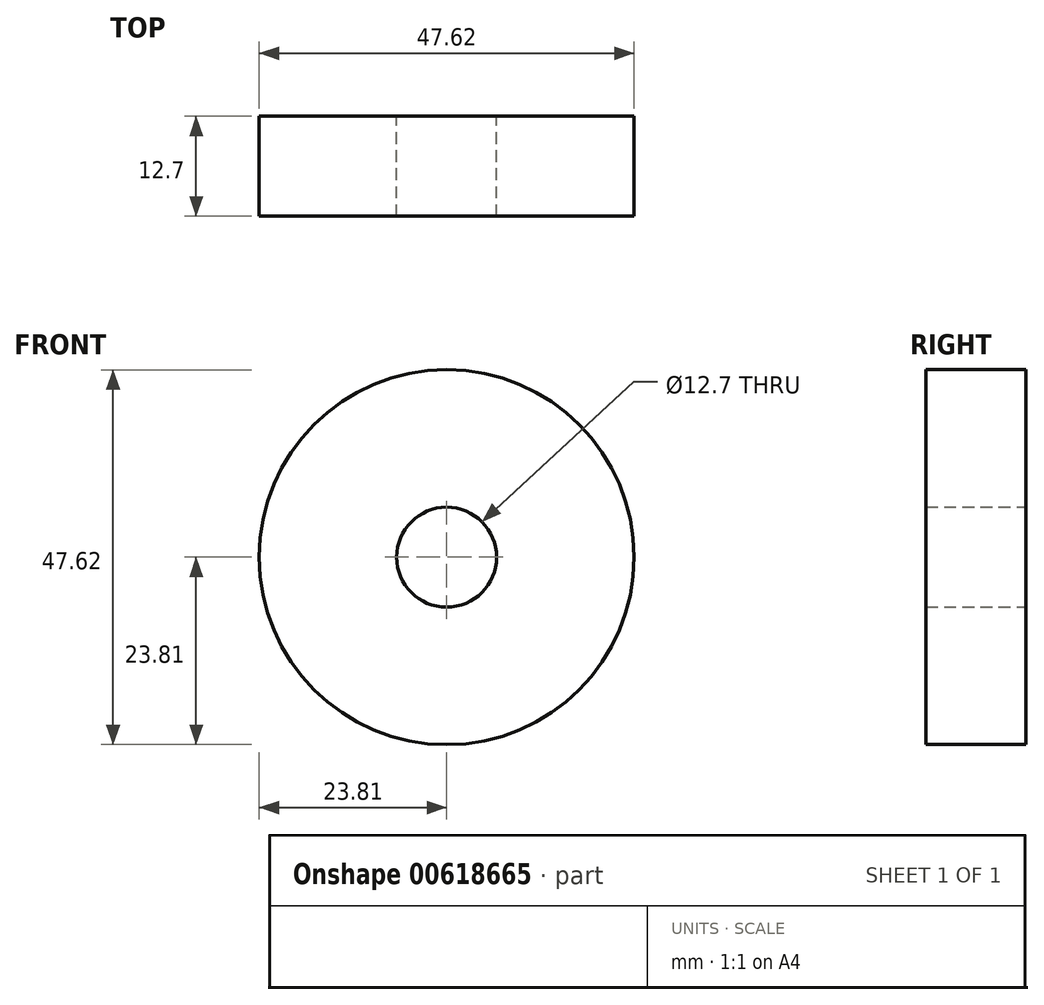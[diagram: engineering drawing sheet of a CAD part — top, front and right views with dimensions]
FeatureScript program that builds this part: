
annotation { "Feature Type Name" : "Feature", "Feature Type Description" : "" }
export const myFeature = defineFeature(function(context is Context, id is Id, definition is map)
    precondition{}
    {
        {
            var Q0;
            Q0=qCreatedBy(makeId("Front.planeOp"),FACE);
            var sketch = newSketch(context, id + "F0", { "sketchPlane" : qUnion([Q0])});
            skCircle(sketch, "E0", {"center": v(0, 0) * mm, "radius": 23.81 * mm});
            skCircle(sketch, "E1", {"center": v(0, 0) * mm, "radius": 6.35 * mm});
            skSolve(sketch);
        }
        {
            var Q0;
            Q0=makeQuery(id+"F0.imprint","IMPRINT",FACE,{"disambiguationData":[TD([[makeQuery(id+"F0.imprint","IMPRINT",EDGE,{"derivedFrom":sQuery(id+"F0.wireOp",EDGE,"E0")}),1.0]])]});
            extrude(context, id + "F1", {"entities" : qUnion([Q0]), "depth" : 12.7 * mm, "offsetDistance" : 25.4 * mm});
        }
    });
